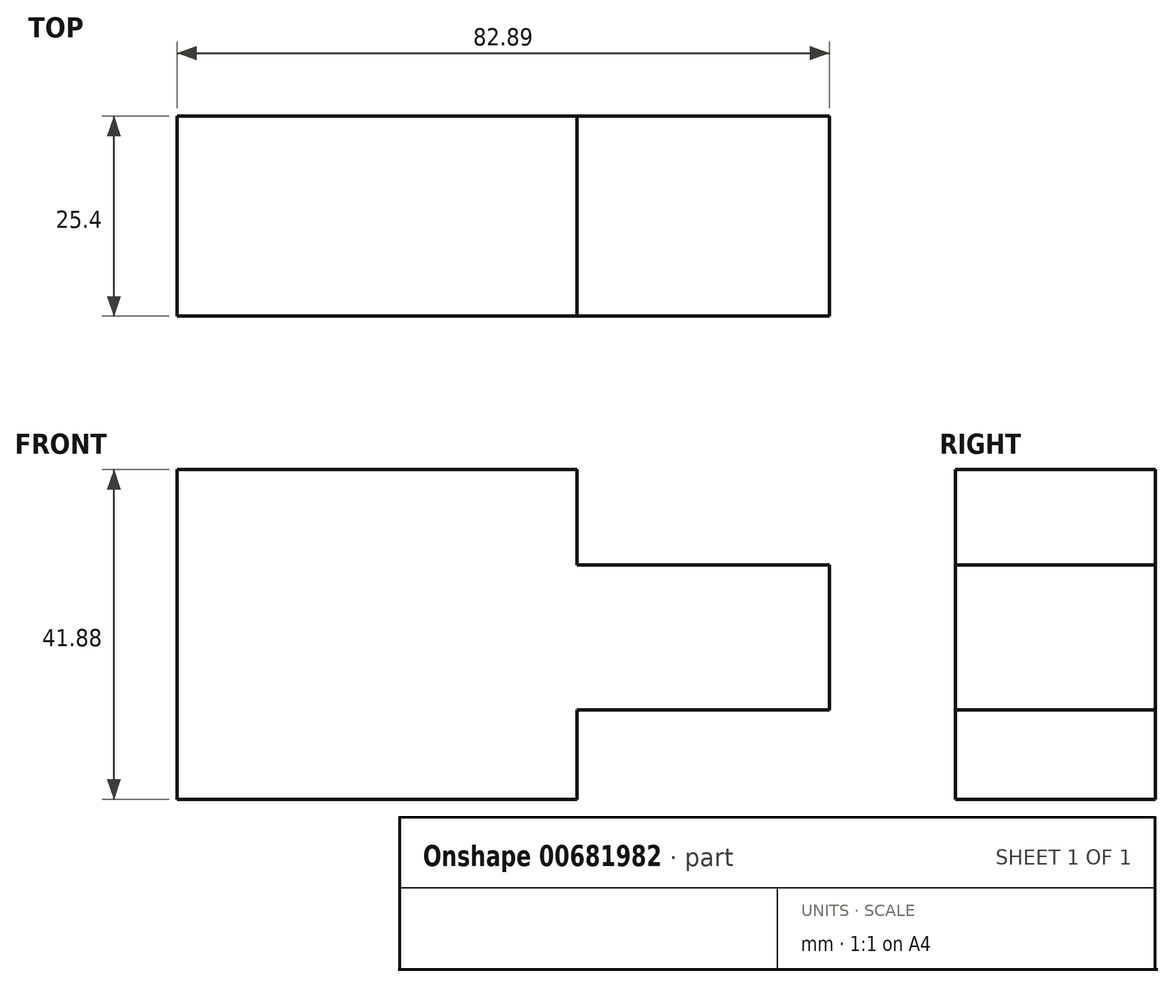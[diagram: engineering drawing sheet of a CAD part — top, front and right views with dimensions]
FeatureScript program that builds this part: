
annotation { "Feature Type Name" : "Feature", "Feature Type Description" : "" }
export const myFeature = defineFeature(function(context is Context, id is Id, definition is map)
    precondition{}
    {
        {
            var Q0;
            Q0=qCreatedBy(makeId("Front.planeOp"),FACE);
            var sketch = newSketch(context, id + "F0", { "sketchPlane" : qUnion([Q0])});
            skLineSegment(sketch, "E0", {"start": v(0, 0) * mm, "end": v(-50.8, 0) * mm});
            skLineSegment(sketch, "E1", {"start": v(-46.77, 0) * mm, "end": v(-50.8, 0) * mm});
            skLineSegment(sketch, "E2", {"start": v(-50.8, 0) * mm, "end": v(-50.8, 41.88) * mm});
            skLineSegment(sketch, "E3", {"start": v(-50.8, 41.88) * mm, "end": v(0, 41.88) * mm});
            skLineSegment(sketch, "E4", {"start": v(0, 41.88) * mm, "end": v(0, 29.79) * mm});
            skLineSegment(sketch, "E5", {"start": v(0, 29.79) * mm, "end": v(32.1, 29.79) * mm});
            skLineSegment(sketch, "E6", {"start": v(32.1, 29.79) * mm, "end": v(32.1, 11.37) * mm});
            skLineSegment(sketch, "E7", {"start": v(32.1, 11.37) * mm, "end": v(0, 11.37) * mm});
            skLineSegment(sketch, "E8", {"start": v(0, 11.37) * mm, "end": v(0, 0) * mm});
            skSolve(sketch);
        }
        {
            var Q0;
            Q0 = qSketchRegion(id + "F0", true);
            extrude(context, id + "F1", {"entities" : qUnion([Q0]), "depth" : 25.4 * mm, "offsetDistance" : 25.4 * mm});
        }
    });
